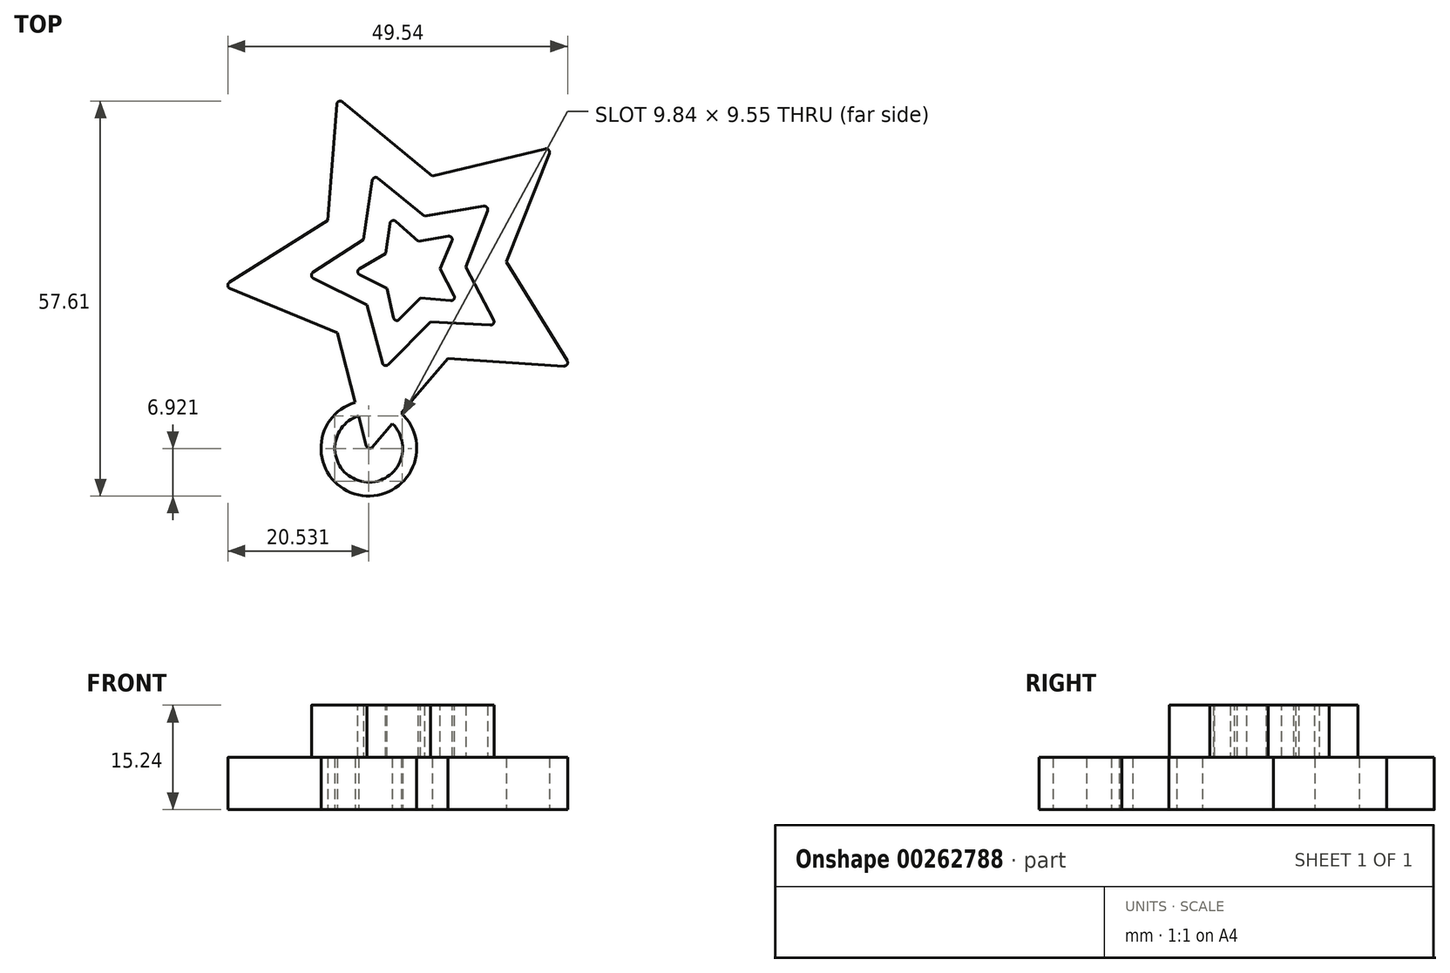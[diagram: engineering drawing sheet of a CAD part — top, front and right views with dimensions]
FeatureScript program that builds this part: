
annotation { "Feature Type Name" : "Feature", "Feature Type Description" : "" }
export const myFeature = defineFeature(function(context is Context, id is Id, definition is map)
    precondition{}
    {
        {
            var Q0;
            Q0=qCreatedBy(makeId("Top.planeOp"),FACE);
            var sketch = newSketch(context, id + "F0", { "sketchPlane" : qUnion([Q0])});
            skPoint(sketch, "E0.0.midPoint", {"position": v(16.12, -9.7) * mm});
            skLineSegment(sketch, "E1", {"start": v(-16.63, 42.18) * mm, "end": v(5.25, 22.65) * mm});
            skLineSegment(sketch, "E2", {"start": v(-17.47, 41.84) * mm, "end": v(-19.92, 11.99) * mm});
            skPoint(sketch, "E3.start.orphan", {"position": v(-7.34, 17.32) * mm});
            skPoint(sketch, "E4", {"position": v(-14.44, 40.22) * mm});
            skPoint(sketch, "E5", {"position": v(-17.7, 39.13) * mm});
            skPoint(sketch, "E6.visualSharp", {"position": v(-17.39, 42.86) * mm});
            skArc(sketch, "E6.filletArc", {"start": v(-16.63, 42.18) * mm, "mid": v(-17.16, 42.27) * mm, "end": v(-17.47, 41.84) * mm});
            skPoint(sketch, "E7.orphan", {"position": v(9.07, -21.4) * mm});
            skPoint(sketch, "E0.4.end.orphan", {"position": v(23.16, 2.01) * mm});
            skLineSegment(sketch, "E8.1.0", {"start": v(-45.2, -3.69) * mm, "end": v(-17.56, -15.24) * mm});
            skLineSegment(sketch, "E8.1.1", {"start": v(-45.25, -2.78) * mm, "end": v(-19.92, 11.99) * mm});
            skPoint(sketch, "E8.1.2", {"position": v(-42.68, -4.74) * mm});
            skPoint(sketch, "E8.1.3", {"position": v(-42.72, -1.3) * mm});
            skPoint(sketch, "E8.1.4", {"position": v(-18.74, -1.63) * mm});
            skPoint(sketch, "E8.1.5", {"position": v(-46.13, -3.3) * mm});
            skArc(sketch, "E8.1.6", {"start": v(-45.25, -2.78) * mm, "mid": v(-45.5, -3.25) * mm, "end": v(-45.2, -3.69) * mm});
            skLineSegment(sketch, "E8.2.0", {"start": v(-10.46, -44.12) * mm, "end": v(9.07, -21.4) * mm});
            skLineSegment(sketch, "E8.2.1", {"start": v(-11.34, -43.9) * mm, "end": v(-17.56, -15.24) * mm});
            skPoint(sketch, "E8.2.2", {"position": v(-8.68, -42.06) * mm});
            skPoint(sketch, "E8.2.3", {"position": v(-11.96, -41.03) * mm});
            skPoint(sketch, "E8.2.4", {"position": v(-4.24, -18.32) * mm});
            skPoint(sketch, "E8.2.5", {"position": v(-11.12, -44.9) * mm});
            skArc(sketch, "E8.2.6", {"start": v(-11.34, -43.9) * mm, "mid": v(-10.97, -44.28) * mm, "end": v(-10.46, -44.12) * mm});
            skLineSegment(sketch, "E8.3.0", {"start": v(38.73, -23.58) * mm, "end": v(23.16, 2.01) * mm});
            skLineSegment(sketch, "E8.3.1", {"start": v(38.24, -24.35) * mm, "end": v(9.07, -21.4) * mm});
            skPoint(sketch, "E8.3.2", {"position": v(37.31, -21.25) * mm});
            skPoint(sketch, "E8.3.3", {"position": v(35.32, -24.05) * mm});
            skPoint(sketch, "E8.3.5", {"position": v(39.26, -24.45) * mm});
            skArc(sketch, "E8.3.6", {"start": v(38.24, -24.35) * mm, "mid": v(38.72, -24.11) * mm, "end": v(38.73, -23.58) * mm});
            skLineSegment(sketch, "E8.4.0", {"start": v(34.4, 29.55) * mm, "end": v(5.25, 22.65) * mm});
            skLineSegment(sketch, "E8.4.1", {"start": v(34.97, 28.85) * mm, "end": v(23.16, 2.01) * mm});
            skPoint(sketch, "E8.4.2", {"position": v(31.74, 28.92) * mm});
            skPoint(sketch, "E8.4.3", {"position": v(33.8, 26.16) * mm});
            skPoint(sketch, "E8.4.4", {"position": v(14.2, 12.33) * mm});
            skPoint(sketch, "E8.4.5", {"position": v(35.39, 29.78) * mm});
            skArc(sketch, "E8.4.6", {"start": v(34.97, 28.85) * mm, "mid": v(34.9, 29.38) * mm, "end": v(34.4, 29.55) * mm});
            skPoint(sketch, "E8.center", {"position": v(0, 0) * mm});
            skSolve(sketch);
        }
        {
            var Q0;
            Q0=makeQuery(id+"F0.imprint","IMPRINT",FACE,{"disambiguationData":[TD([[makeQuery(id+"F0.imprint","IMPRINT",EDGE,{"derivedFrom":sQuery(id+"F0.wireOp",EDGE,"E1")}),-1.0]])]});
            extrude(context, id + "F1", {"entities" : qUnion([Q0]), "depth" : 7.62 * mm});
        }
        {
            var Q0;
            Q0=makeQuery(id+"F1.opExtrude","CAP_FACE",FACE,{"disambiguationData":[OSD([sQuery(id+"F0.wireOp",EDGE,"E1"),sQuery(id+"F0.wireOp",EDGE,"E2"),sQuery(id+"F0.wireOp",EDGE,"E6.filletArc"),sQuery(id+"F0.wireOp",EDGE,"E8.1.0"),sQuery(id+"F0.wireOp",EDGE,"E8.1.1"),sQuery(id+"F0.wireOp",EDGE,"E8.1.6"),sQuery(id+"F0.wireOp",EDGE,"E8.2.0"),sQuery(id+"F0.wireOp",EDGE,"E8.2.1"),sQuery(id+"F0.wireOp",EDGE,"E8.2.6"),sQuery(id+"F0.wireOp",EDGE,"E8.3.0"),sQuery(id+"F0.wireOp",EDGE,"E8.3.1"),sQuery(id+"F0.wireOp",EDGE,"E8.3.6"),sQuery(id+"F0.wireOp",EDGE,"E8.4.0"),sQuery(id+"F0.wireOp",EDGE,"E8.4.1"),sQuery(id+"F0.wireOp",EDGE,"E8.4.6")])],"isStart":false});
            var sketch = newSketch(context, id + "F2", { "sketchPlane" : qUnion([Q0])});
            skPoint(sketch, "E9.0.midPoint", {"position": v(-4.42, 10.46) * mm});
            skLineSegment(sketch, "E10", {"start": v(-10.63, 25.14) * mm, "end": v(-12.02, 7.25) * mm, "construction": true});
            skLineSegment(sketch, "E11", {"start": v(-10.63, 25.14) * mm, "end": v(3.18, 13.68) * mm, "construction": true});
            skLineSegment(sketch, "E12", {"start": v(-12.02, 7.25) * mm, "end": v(-10.7, 24.16) * mm});
            skLineSegment(sketch, "E13", {"start": v(3.18, 13.68) * mm, "end": v(-9.88, 24.51) * mm});
            skPoint(sketch, "E14", {"position": v(-10.76, 23.53) * mm});
            skPoint(sketch, "E15", {"position": v(-9.41, 24.13) * mm});
            skPoint(sketch, "E16.visualSharp", {"position": v(-10.63, 25.14) * mm});
            skArc(sketch, "E16.filletArc", {"start": v(-9.88, 24.51) * mm, "mid": v(-10.4, 24.6) * mm, "end": v(-10.7, 24.16) * mm});
            skLineSegment(sketch, "E17.1.0", {"start": v(-27.2, -2.34) * mm, "end": v(-12.02, 7.25) * mm, "construction": true});
            skPoint(sketch, "E17.1.1", {"position": v(-25.86, -1.5) * mm});
            skPoint(sketch, "E17.1.2", {"position": v(-25.7, -2.96) * mm});
            skLineSegment(sketch, "E17.1.3", {"start": v(-27.2, -2.34) * mm, "end": v(-10.6, -9.2) * mm, "construction": true});
            skPoint(sketch, "E17.1.4", {"position": v(-11.32, -0.98) * mm});
            skLineSegment(sketch, "E17.1.5", {"start": v(-12.02, 7.25) * mm, "end": v(-26.37, -1.82) * mm});
            skLineSegment(sketch, "E17.1.6", {"start": v(-10.6, -9.2) * mm, "end": v(-26.3, -2.72) * mm});
            skPoint(sketch, "E17.1.7", {"position": v(-27.2, -2.34) * mm});
            skArc(sketch, "E17.1.8", {"start": v(-26.37, -1.82) * mm, "mid": v(-26.6, -2.3) * mm, "end": v(-26.3, -2.72) * mm});
            skLineSegment(sketch, "E17.2.0", {"start": v(-6.18, -26.6) * mm, "end": v(-10.6, -9.2) * mm, "construction": true});
            skPoint(sketch, "E17.2.1", {"position": v(-6.57, -25.05) * mm});
            skPoint(sketch, "E17.2.2", {"position": v(-5.13, -25.36) * mm});
            skLineSegment(sketch, "E17.2.3", {"start": v(-6.18, -26.6) * mm, "end": v(5.47, -12.93) * mm, "construction": true});
            skPoint(sketch, "E17.2.4", {"position": v(-2.57, -11.06) * mm});
            skLineSegment(sketch, "E17.2.5", {"start": v(-10.6, -9.2) * mm, "end": v(-6.42, -25.64) * mm});
            skLineSegment(sketch, "E17.2.6", {"start": v(5.47, -12.93) * mm, "end": v(-5.54, -25.84) * mm});
            skPoint(sketch, "E17.2.7", {"position": v(-6.18, -26.6) * mm});
            skArc(sketch, "E17.2.8", {"start": v(-6.42, -25.64) * mm, "mid": v(-6.04, -26) * mm, "end": v(-5.54, -25.84) * mm});
            skLineSegment(sketch, "E17.3.0", {"start": v(23.38, -14.09) * mm, "end": v(5.47, -12.93) * mm, "construction": true});
            skPoint(sketch, "E17.3.1", {"position": v(21.8, -13.99) * mm});
            skPoint(sketch, "E17.3.2", {"position": v(22.53, -12.71) * mm});
            skLineSegment(sketch, "E17.3.3", {"start": v(23.38, -14.09) * mm, "end": v(13.99, 1.2) * mm, "construction": true});
            skPoint(sketch, "E17.3.4", {"position": v(9.73, -5.86) * mm});
            skLineSegment(sketch, "E17.3.5", {"start": v(5.47, -12.93) * mm, "end": v(22.4, -14.03) * mm});
            skLineSegment(sketch, "E17.3.6", {"start": v(13.99, 1.2) * mm, "end": v(22.87, -13.25) * mm});
            skPoint(sketch, "E17.3.7", {"position": v(23.38, -14.09) * mm});
            skArc(sketch, "E17.3.8", {"start": v(22.4, -14.03) * mm, "mid": v(22.87, -13.78) * mm, "end": v(22.87, -13.25) * mm});
            skLineSegment(sketch, "E17.4.0", {"start": v(20.63, 17.88) * mm, "end": v(13.99, 1.2) * mm, "construction": true});
            skPoint(sketch, "E17.4.1", {"position": v(20.04, 16.4) * mm});
            skPoint(sketch, "E17.4.2", {"position": v(19.05, 17.5) * mm});
            skLineSegment(sketch, "E17.4.3", {"start": v(20.63, 17.88) * mm, "end": v(3.18, 13.68) * mm, "construction": true});
            skPoint(sketch, "E17.4.4", {"position": v(8.58, 7.44) * mm});
            skLineSegment(sketch, "E17.4.5", {"start": v(13.99, 1.2) * mm, "end": v(20.26, 16.97) * mm});
            skLineSegment(sketch, "E17.4.6", {"start": v(3.18, 13.68) * mm, "end": v(19.67, 17.65) * mm});
            skPoint(sketch, "E17.4.7", {"position": v(20.63, 17.88) * mm});
            skArc(sketch, "E17.4.8", {"start": v(20.26, 16.97) * mm, "mid": v(20.17, 17.5) * mm, "end": v(19.67, 17.65) * mm});
            skPoint(sketch, "E17.center", {"position": v(0, 0) * mm});
            skSolve(sketch);
        }
        {
            var Q0;
            Q0=makeQuery(id+"F2.imprint","IMPRINT",FACE,{"disambiguationData":[TD([[makeQuery(id+"F2.imprint","IMPRINT",EDGE,{"derivedFrom":sQuery(id+"F2.wireOp",EDGE,"E12")}),-1.0]])]});
            extrude(context, id + "F3", {"entities" : qUnion([Q0]), "operationType" : NewBodyOperationType.ADD, "depth" : 7.62 * mm});
        }
        {
            var Q0;
            Q0=makeQuery(id+"F3.opExtrude","CAP_FACE",FACE,{"disambiguationData":[OSD([sQuery(id+"F2.wireOp",EDGE,"E12"),sQuery(id+"F2.wireOp",EDGE,"E13"),sQuery(id+"F2.wireOp",EDGE,"E16.filletArc"),sQuery(id+"F2.wireOp",EDGE,"E17.1.5"),sQuery(id+"F2.wireOp",EDGE,"E17.1.6"),sQuery(id+"F2.wireOp",EDGE,"E17.1.8"),sQuery(id+"F2.wireOp",EDGE,"E17.2.5"),sQuery(id+"F2.wireOp",EDGE,"E17.2.6"),sQuery(id+"F2.wireOp",EDGE,"E17.2.8"),sQuery(id+"F2.wireOp",EDGE,"E17.3.5"),sQuery(id+"F2.wireOp",EDGE,"E17.3.6"),sQuery(id+"F2.wireOp",EDGE,"E17.3.8"),sQuery(id+"F2.wireOp",EDGE,"E17.4.5"),sQuery(id+"F2.wireOp",EDGE,"E17.4.6"),sQuery(id+"F2.wireOp",EDGE,"E17.4.8")])],"isStart":false});
            var sketch = newSketch(context, id + "F4", { "sketchPlane" : qUnion([Q0])});
            skPoint(sketch, "E18.0.midPoint", {"position": v(-1.68, 4.35) * mm});
            skPoint(sketch, "E19.orphan", {"position": v(-4.84, 3.12) * mm});
            skPoint(sketch, "E20.orphan", {"position": v(2.08, -5.37) * mm});
            skPoint(sketch, "E18.0.end.orphan", {"position": v(1.47, 5.57) * mm});
            skPoint(sketch, "E21.0.midPoint", {"position": v(-2.37, 6.12) * mm});
            skLineSegment(sketch, "E22", {"start": v(-5.53, 13.06) * mm, "end": v(-6.82, 4.4) * mm});
            skLineSegment(sketch, "E23", {"start": v(-4.7, 13.37) * mm, "end": v(2.08, 7.85) * mm});
            skPoint(sketch, "E24", {"position": v(-5.58, 12.74) * mm});
            skPoint(sketch, "E25", {"position": v(-4.52, 13.22) * mm});
            skPoint(sketch, "E26.visualSharp", {"position": v(-5.4, 13.94) * mm});
            skArc(sketch, "E26.filletArc", {"start": v(-4.7, 13.37) * mm, "mid": v(-5.2, 13.45) * mm, "end": v(-5.53, 13.06) * mm});
            skLineSegment(sketch, "E27.1.0", {"start": v(-14.12, -1.22) * mm, "end": v(-6.3, -5.13) * mm});
            skPoint(sketch, "E27.1.1", {"position": v(-14.92, -0.83) * mm});
            skPoint(sketch, "E27.1.2", {"position": v(-13.97, -0.21) * mm});
            skLineSegment(sketch, "E27.1.3", {"start": v(-14.17, -0.34) * mm, "end": v(-6.82, 4.4) * mm});
            skPoint(sketch, "E27.1.4", {"position": v(-13.84, -1.37) * mm});
            skArc(sketch, "E27.1.5", {"start": v(-14.17, -0.34) * mm, "mid": v(-14.4, -0.8) * mm, "end": v(-14.12, -1.22) * mm});
            skLineSegment(sketch, "E27.2.0", {"start": v(-3.2, -13.81) * mm, "end": v(2.93, -7.57) * mm});
            skPoint(sketch, "E27.2.1", {"position": v(-3.83, -14.45) * mm});
            skPoint(sketch, "E27.2.2", {"position": v(-4.12, -13.36) * mm});
            skLineSegment(sketch, "E27.2.3", {"start": v(-4.06, -13.59) * mm, "end": v(-6.3, -5.13) * mm});
            skPoint(sketch, "E27.2.4", {"position": v(-2.98, -13.58) * mm});
            skArc(sketch, "E27.2.5", {"start": v(-4.06, -13.59) * mm, "mid": v(-3.7, -13.95) * mm, "end": v(-3.2, -13.81) * mm});
            skLineSegment(sketch, "E27.3.0", {"start": v(12.15, -7.31) * mm, "end": v(8.1, 0.45) * mm});
            skPoint(sketch, "E27.3.1", {"position": v(12.56, -8.1) * mm});
            skPoint(sketch, "E27.3.2", {"position": v(11.43, -8.04) * mm});
            skLineSegment(sketch, "E27.3.3", {"start": v(11.67, -8.05) * mm, "end": v(2.93, -7.57) * mm});
            skPoint(sketch, "E27.3.4", {"position": v(12, -7.03) * mm});
            skArc(sketch, "E27.3.5", {"start": v(11.67, -8.05) * mm, "mid": v(12.12, -7.82) * mm, "end": v(12.15, -7.31) * mm});
            skLineSegment(sketch, "E27.4.0", {"start": v(10.7, 9.3) * mm, "end": v(2.08, 7.85) * mm});
            skPoint(sketch, "E27.4.1", {"position": v(11.59, 9.44) * mm});
            skPoint(sketch, "E27.4.2", {"position": v(11.18, 8.39) * mm});
            skLineSegment(sketch, "E27.4.3", {"start": v(11.27, 8.6) * mm, "end": v(8.1, 0.45) * mm});
            skPoint(sketch, "E27.4.4", {"position": v(10.4, 9.24) * mm});
            skArc(sketch, "E27.4.5", {"start": v(11.27, 8.6) * mm, "mid": v(11.19, 9.11) * mm, "end": v(10.7, 9.3) * mm});
            skPoint(sketch, "E27.center", {"position": v(0, 0) * mm});
            skSolve(sketch);
        }
        {
            var Q0;
            Q0=makeQuery(id+"F4.imprint","IMPRINT",FACE,{"disambiguationData":[TD([[makeQuery(id+"F4.imprint","IMPRINT",EDGE,{"derivedFrom":sQuery(id+"F4.wireOp",EDGE,"E22")}),1.0]])]});
            extrude(context, id + "F5", {"entities" : qUnion([Q0]), "operationType" : NewBodyOperationType.ADD, "depth" : 7.62 * mm});
        }
        {
            var Q0;
            Q0=makeQuery(id+"F5.opExtrude","CAP_FACE",FACE,{"disambiguationData":[OSD([sQuery(id+"F4.wireOp",EDGE,"E22"),sQuery(id+"F4.wireOp",EDGE,"E23"),sQuery(id+"F4.wireOp",EDGE,"E26.filletArc"),sQuery(id+"F4.wireOp",EDGE,"E27.1.0"),sQuery(id+"F4.wireOp",EDGE,"E27.1.3"),sQuery(id+"F4.wireOp",EDGE,"E27.1.5"),sQuery(id+"F4.wireOp",EDGE,"E27.2.0"),sQuery(id+"F4.wireOp",EDGE,"E27.2.3"),sQuery(id+"F4.wireOp",EDGE,"E27.2.5"),sQuery(id+"F4.wireOp",EDGE,"E27.3.0"),sQuery(id+"F4.wireOp",EDGE,"E27.3.3"),sQuery(id+"F4.wireOp",EDGE,"E27.3.5"),sQuery(id+"F4.wireOp",EDGE,"E27.4.0"),sQuery(id+"F4.wireOp",EDGE,"E27.4.3"),sQuery(id+"F4.wireOp",EDGE,"E27.4.5")])],"isStart":false});
            var sketch = newSketch(context, id + "F6", { "sketchPlane" : qUnion([Q0])});
            skSolve(sketch);
        }
        {
            var Q0;
            Q0=makeQuery(id+"F6.imprint","IMPRINT",FACE,{"disambiguationData":[TD([[makeQuery(id+"F6.imprint","IMPRINT",EDGE,{"derivedFrom":makeQuery(id+"F5.opExtrude","CAP_EDGE",EDGE,{"disambiguationData":[OSD([sQuery(id+"F4.wireOp",EDGE,"E22")])],"isStart":false})}),1.0]])]});
            var sketch = newSketch(context, id + "F7", { "sketchPlane" : qUnion([Q0])});
            skSolve(sketch);
        }
        {
            var Q0;
            Q0 = qSketchRegion(id + "F7", true);
            var Q1;
            Q1=makeQuery(id+"F1.opExtrude","CAP_FACE",FACE,{"disambiguationData":[OSD([sQuery(id+"F0.wireOp",EDGE,"E1"),sQuery(id+"F0.wireOp",EDGE,"E2"),sQuery(id+"F0.wireOp",EDGE,"E6.filletArc"),sQuery(id+"F0.wireOp",EDGE,"E8.1.0"),sQuery(id+"F0.wireOp",EDGE,"E8.1.1"),sQuery(id+"F0.wireOp",EDGE,"E8.1.6"),sQuery(id+"F0.wireOp",EDGE,"E8.2.0"),sQuery(id+"F0.wireOp",EDGE,"E8.2.1"),sQuery(id+"F0.wireOp",EDGE,"E8.2.6"),sQuery(id+"F0.wireOp",EDGE,"E8.3.0"),sQuery(id+"F0.wireOp",EDGE,"E8.3.1"),sQuery(id+"F0.wireOp",EDGE,"E8.3.6"),sQuery(id+"F0.wireOp",EDGE,"E8.4.0"),sQuery(id+"F0.wireOp",EDGE,"E8.4.1"),sQuery(id+"F0.wireOp",EDGE,"E8.4.6")])],"isStart":true});
            extrude(context, id + "F8", {"entities" : qUnion([Q0, Q1]), "operationType" : NewBodyOperationType.REMOVE, "oppositeDirection" : true, "depth" : 7.62 * mm});
        }
        {
            var Q0;
            Q0=makeQuery(id+"F7.imprint","IMPRINT",FACE,{"disambiguationData":[TD([[makeQuery(id+"F7.imprint","IMPRINT",EDGE,{"derivedFrom":makeQuery(id+"F6.imprint","IMPRINT",EDGE,{"derivedFrom":makeQuery(id+"F5.opExtrude","CAP_EDGE",EDGE,{"disambiguationData":[OSD([sQuery(id+"F4.wireOp",EDGE,"E22")])],"isStart":false})})}),1.0]])]});
            var sketch = newSketch(context, id + "F9", { "sketchPlane" : qUnion([Q0])});
            skPoint(sketch, "E28.0.midPoint", {"position": v(-1.2, 3.28) * mm});
            skLineSegment(sketch, "E29", {"start": v(-2.96, 6.78) * mm, "end": v(-3.59, 2.4) * mm});
            skLineSegment(sketch, "E30", {"start": v(1.18, 4.16) * mm, "end": v(-2.12, 7.09) * mm});
            skPoint(sketch, "E31", {"position": v(-2.9, 7.21) * mm});
            skPoint(sketch, "E32", {"position": v(-2.48, 7.4) * mm});
            skPoint(sketch, "E33.visualSharp", {"position": v(-2.83, 7.71) * mm});
            skArc(sketch, "E33.filletArc", {"start": v(-2.12, 7.09) * mm, "mid": v(-2.63, 7.18) * mm, "end": v(-2.96, 6.78) * mm});
            skPoint(sketch, "E34.1.0", {"position": v(-3.5, -0.13) * mm});
            skPoint(sketch, "E34.1.1", {"position": v(-8.2, -0.3) * mm});
            skPoint(sketch, "E34.1.2", {"position": v(-7.76, -0.53) * mm});
            skLineSegment(sketch, "E34.1.3", {"start": v(-7.36, -0.72) * mm, "end": v(-3.4, -2.67) * mm});
            skLineSegment(sketch, "E34.1.4", {"start": v(-3.59, 2.4) * mm, "end": v(-7.4, 0.17) * mm});
            skPoint(sketch, "E34.1.5", {"position": v(-7.8, -0.07) * mm});
            skArc(sketch, "E34.1.6", {"start": v(-7.4, 0.17) * mm, "mid": v(-7.64, -0.28) * mm, "end": v(-7.36, -0.72) * mm});
            skPoint(sketch, "E34.2.0", {"position": v(-0.96, -3.36) * mm});
            skPoint(sketch, "E34.2.1", {"position": v(-2.25, -7.9) * mm});
            skPoint(sketch, "E34.2.2", {"position": v(-1.9, -7.54) * mm});
            skLineSegment(sketch, "E34.2.3", {"start": v(-1.59, -7.22) * mm, "end": v(1.49, -4.06) * mm});
            skLineSegment(sketch, "E34.2.4", {"start": v(-3.4, -2.67) * mm, "end": v(-2.45, -6.98) * mm});
            skPoint(sketch, "E34.2.5", {"position": v(-2.35, -7.45) * mm});
            skArc(sketch, "E34.2.6", {"start": v(-2.45, -6.98) * mm, "mid": v(-2.1, -7.36) * mm, "end": v(-1.59, -7.22) * mm});
            skPoint(sketch, "E34.3.0", {"position": v(2.9, -1.95) * mm});
            skPoint(sketch, "E34.3.1", {"position": v(6.82, -4.58) * mm});
            skPoint(sketch, "E34.3.2", {"position": v(6.58, -4.13) * mm});
            skLineSegment(sketch, "E34.3.3", {"start": v(6.38, -3.74) * mm, "end": v(4.32, 0.16) * mm});
            skLineSegment(sketch, "E34.3.4", {"start": v(1.49, -4.06) * mm, "end": v(5.88, -4.49) * mm});
            skPoint(sketch, "E34.3.5", {"position": v(6.36, -4.53) * mm});
            skArc(sketch, "E34.3.6", {"start": v(5.88, -4.49) * mm, "mid": v(6.35, -4.26) * mm, "end": v(6.38, -3.74) * mm});
            skPoint(sketch, "E34.4.0", {"position": v(2.75, 2.16) * mm});
            skPoint(sketch, "E34.4.1", {"position": v(6.46, 5.07) * mm});
            skPoint(sketch, "E34.4.2", {"position": v(5.97, 4.98) * mm});
            skLineSegment(sketch, "E34.4.3", {"start": v(5.53, 4.9) * mm, "end": v(1.18, 4.16) * mm});
            skLineSegment(sketch, "E34.4.4", {"start": v(4.32, 0.16) * mm, "end": v(6.08, 4.2) * mm});
            skPoint(sketch, "E34.4.5", {"position": v(6.28, 4.65) * mm});
            skArc(sketch, "E34.4.6", {"start": v(6.08, 4.2) * mm, "mid": v(6.02, 4.72) * mm, "end": v(5.53, 4.9) * mm});
            skPoint(sketch, "E34.center", {"position": v(0, 0) * mm});
            skSolve(sketch);
        }
        {
            var Q0;
            Q0=makeQuery(id+"F9.imprint","IMPRINT",FACE,{"disambiguationData":[TD([[makeQuery(id+"F9.imprint","IMPRINT",EDGE,{"derivedFrom":sQuery(id+"F9.wireOp",EDGE,"E29")}),1.0]])]});
            extrude(context, id + "F10", {"entities" : qUnion([Q0]), "operationType" : NewBodyOperationType.REMOVE, "oppositeDirection" : true, "depth" : 7.62 * mm});
        }
        {
            var Q0;
            Q0=makeQuery(id+"F8.boolean.opBoolean","COPY",FACE,{"derivedFrom":makeQuery(id+"F8.opExtrude","CAP_FACE",FACE,{"disambiguationData":[OSD([sQuery(id+"F0.wireOp",EDGE,"E1"),sQuery(id+"F0.wireOp",EDGE,"E2"),sQuery(id+"F0.wireOp",EDGE,"E6.filletArc"),sQuery(id+"F0.wireOp",EDGE,"E8.1.0"),sQuery(id+"F0.wireOp",EDGE,"E8.1.1"),sQuery(id+"F0.wireOp",EDGE,"E8.1.6"),sQuery(id+"F0.wireOp",EDGE,"E8.2.0"),sQuery(id+"F0.wireOp",EDGE,"E8.2.1"),sQuery(id+"F0.wireOp",EDGE,"E8.2.6"),sQuery(id+"F0.wireOp",EDGE,"E8.3.0"),sQuery(id+"F0.wireOp",EDGE,"E8.3.1"),sQuery(id+"F0.wireOp",EDGE,"E8.3.6"),sQuery(id+"F0.wireOp",EDGE,"E8.4.0"),sQuery(id+"F0.wireOp",EDGE,"E8.4.1"),sQuery(id+"F0.wireOp",EDGE,"E8.4.6")])],"isStart":false})});
            var sketch = newSketch(context, id + "F11", { "sketchPlane" : qUnion([Q0])});
            skPoint(sketch, "E35.centerSnap0", {"position": v(-6.04, 26) * mm});
            skPoint(sketch, "E35.center.orphan", {"position": v(-6.42, 26) * mm});
            skPoint(sketch, "E36", {"position": v(-6.8, 24.16) * mm});
            skPoint(sketch, "E37", {"position": v(-7.12, 22.9) * mm});
            skPoint(sketch, "E38", {"position": v(-4.55, 24.68) * mm});
            skPoint(sketch, "E39", {"position": v(-3.7, 23.68) * mm});
            skArc(sketch, "E40", {"start": v(-1.3, 20.88) * mm, "mid": v(-7.62, 32.8) * mm, "end": v(-8.03, 19.32) * mm});
            skArc(sketch, "E41", {"start": v(-2.62, 22.42) * mm, "mid": v(-7.16, 30.83) * mm, "end": v(-7.53, 21.28) * mm});
            skPoint(sketch, "E42", {"position": v(-7.53, 21.28) * mm});
            skPoint(sketch, "E43", {"position": v(-8.03, 19.32) * mm});
            skPoint(sketch, "E44", {"position": v(-2.62, 22.42) * mm});
            skPoint(sketch, "E45", {"position": v(-1.3, 20.88) * mm});
            skSolve(sketch);
        }
        {
            var Q0;
            {var subQ0=sQuery(id+"F11.wireOp",EDGE,"2T3BSztl-Z2dr-GXuw-ZTr2-h5s30eveYY9x");Q0=makeQuery(id+"F11.imprint","IMPRINT",FACE,{"disambiguationData":[TD([[makeQuery(id+"F11.imprint","IMPRINT",EDGE,{"derivedFrom":subQ0}),1.0]])]});}
            var Q1;
            {var subQ0=sQuery(id+"F11.wireOp",EDGE,"E40");Q1=makeQuery(id+"F11.imprint","IMPRINT",FACE,{"disambiguationData":[TD([[makeQuery(id+"F11.imprint","IMPRINT",EDGE,{"derivedFrom":subQ0}),1.0]])]});}
            extrude(context, id + "F12", {"entities" : qUnion([Q0, Q1]), "operationType" : NewBodyOperationType.ADD, "oppositeDirection" : true, "depth" : 7.62 * mm});
        }
    });
